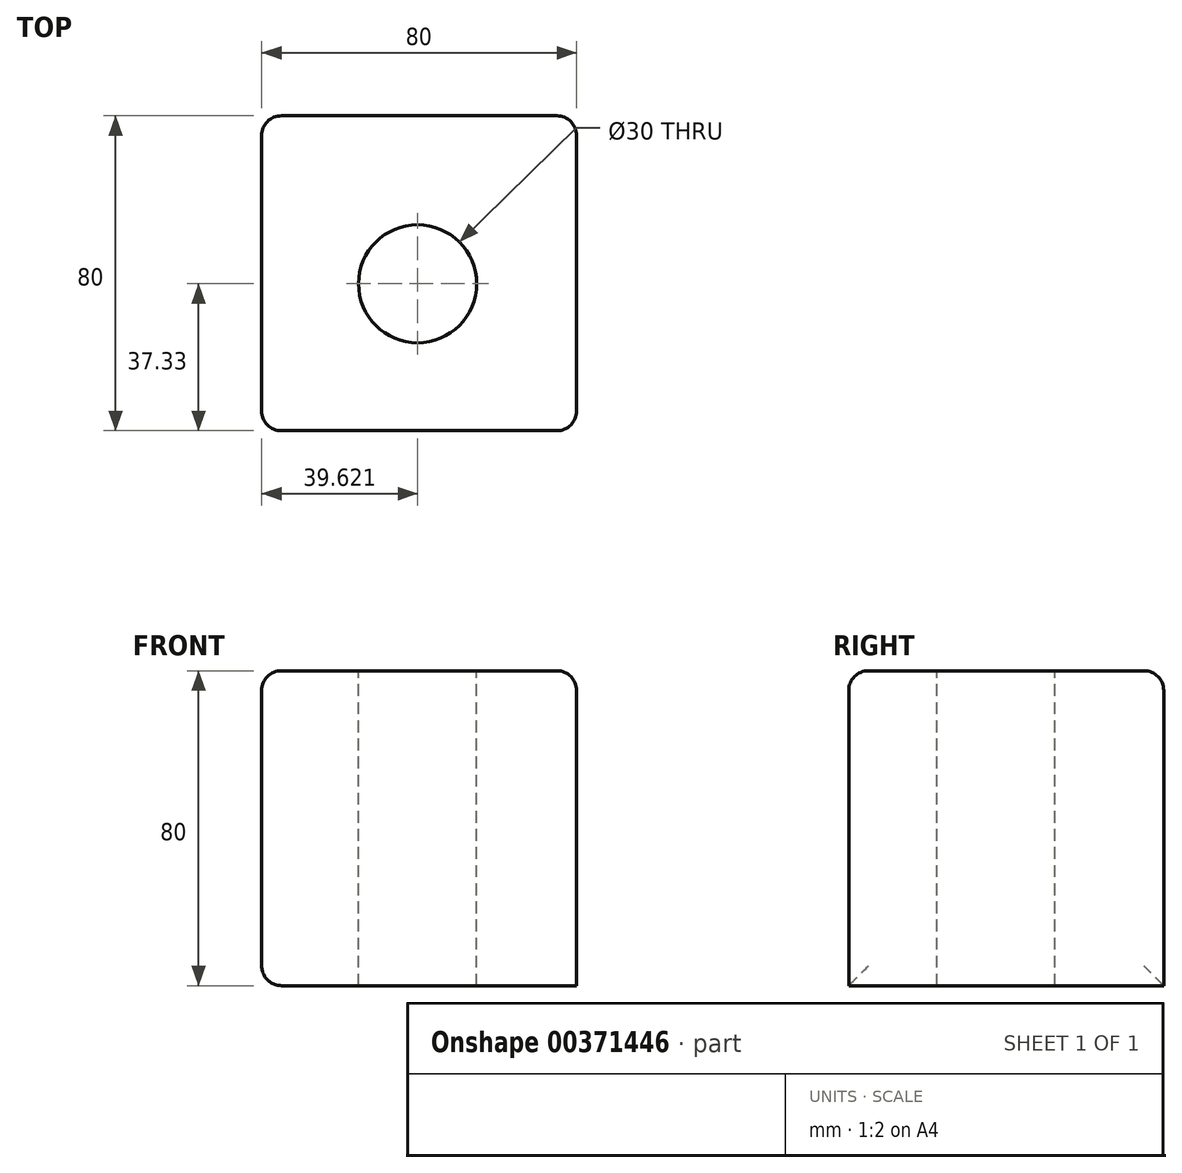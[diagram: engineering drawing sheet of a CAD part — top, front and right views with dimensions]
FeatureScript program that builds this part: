
annotation { "Feature Type Name" : "Feature", "Feature Type Description" : "" }
export const myFeature = defineFeature(function(context is Context, id is Id, definition is map)
    precondition{}
    {
        {
            var Q0;
            Q0=qCreatedBy(makeId("Top.planeOp"),FACE);
            var sketch = newSketch(context, id + "F0", { "sketchPlane" : qUnion([Q0])});
            skLineSegment(sketch, "E0.bottom", {"start": v(-59.3, 42.67) * mm, "end": v(20.7, 42.67) * mm});
            skLineSegment(sketch, "E0.top", {"start": v(-59.3, -37.33) * mm, "end": v(20.7, -37.33) * mm});
            skLineSegment(sketch, "E0.left", {"start": v(-59.3, 42.67) * mm, "end": v(-59.3, -37.33) * mm});
            skLineSegment(sketch, "E0.right", {"start": v(20.7, 42.67) * mm, "end": v(20.7, -37.33) * mm});
            skSolve(sketch);
        }
        {
            var Q0;
            Q0=makeQuery(id+"F0.imprint","IMPRINT",FACE,{"disambiguationData":[TD([[makeQuery(id+"F0.imprint","IMPRINT",EDGE,{"derivedFrom":sQuery(id+"F0.wireOp",EDGE,"E0.bottom")}),-1.0]])]});
            extrude(context, id + "F1", {"entities" : qUnion([Q0]), "depth" : 80 * mm});
        }
        {
            var Q0;
            Q0=makeQuery(id+"F1.opExtrude","CAP_FACE",FACE,{"disambiguationData":[OSD([sQuery(id+"F0.wireOp",EDGE,"E0.bottom"),sQuery(id+"F0.wireOp",EDGE,"E0.top"),sQuery(id+"F0.wireOp",EDGE,"E0.left"),sQuery(id+"F0.wireOp",EDGE,"E0.right")])],"isStart":false});
            var sketch = newSketch(context, id + "F2", { "sketchPlane" : qUnion([Q0])});
            skCircle(sketch, "E1", {"center": v(-19.67, 0) * mm, "radius": 15 * mm});
            skSolve(sketch);
        }
        {
            var Q0;
            Q0=makeQuery(id+"F2.imprint","IMPRINT",FACE,{"disambiguationData":[TD([[makeQuery(id+"F2.imprint","IMPRINT",EDGE,{"derivedFrom":sQuery(id+"F2.wireOp",EDGE,"E1")}),1.0]])]});
            extrude(context, id + "F3", {"entities" : qUnion([Q0]), "operationType" : NewBodyOperationType.REMOVE, "endBound" : BoundingType.THROUGH_ALL, "oppositeDirection" : true, "depth" : 25 * mm});
        }
        {
            var Q0;
            Q0=makeQuery(id+"F1.opExtrude","CAP_EDGE",EDGE,{"disambiguationData":[OSD([sQuery(id+"F0.wireOp",EDGE,"E0.bottom")])],"isStart":false});
            var Q1;
            Q1=makeQuery(id+"F1.opExtrude","CAP_EDGE",EDGE,{"disambiguationData":[OSD([sQuery(id+"F0.wireOp",EDGE,"E0.left")])],"isStart":false});
            var Q2;
            Q2=makeQuery(id+"F1.opExtrude","CAP_EDGE",EDGE,{"disambiguationData":[OSD([sQuery(id+"F0.wireOp",EDGE,"E0.top")])],"isStart":false});
            var Q3;
            Q3=makeQuery(id+"F1.opExtrude","SWEPT_EDGE",EDGE,{"disambiguationData":[OSD([sQuery(id+"F0.wireOp",EDGE,"E0.bottom"),sQuery(id+"F0.wireOp",EDGE,"E0.left")])]});
            var Q4;
            Q4=makeQuery(id+"F1.opExtrude","SWEPT_EDGE",EDGE,{"disambiguationData":[OSD([sQuery(id+"F0.wireOp",EDGE,"E0.top"),sQuery(id+"F0.wireOp",EDGE,"E0.left")])]});
            var Q5;
            Q5=makeQuery(id+"F1.opExtrude","SWEPT_FACE",FACE,{"disambiguationData":[OSD([sQuery(id+"F0.wireOp",EDGE,"E0.left")])]});
            var Q6;
            Q6=makeQuery(id+"F1.opExtrude","SWEPT_EDGE",EDGE,{"disambiguationData":[OSD([sQuery(id+"F0.wireOp",EDGE,"E0.bottom"),sQuery(id+"F0.wireOp",EDGE,"E0.right")])]});
            var Q7;
            Q7=makeQuery(id+"F1.opExtrude","SWEPT_EDGE",EDGE,{"disambiguationData":[OSD([sQuery(id+"F0.wireOp",EDGE,"E0.top"),sQuery(id+"F0.wireOp",EDGE,"E0.right")])]});
            var Q8;
            Q8=makeQuery(id+"F1.opExtrude","CAP_EDGE",EDGE,{"disambiguationData":[OSD([sQuery(id+"F0.wireOp",EDGE,"E0.right")])],"isStart":false});
            fillet(context, id + "F4", {"entities" : qUnion([Q0, Q1, Q2, Q3, Q4, Q5, Q6, Q7, Q8]), "radius" : 5 * mm, "tangentPropagation" : true, "allowEdgeOverflow" : false});
        }
    });
